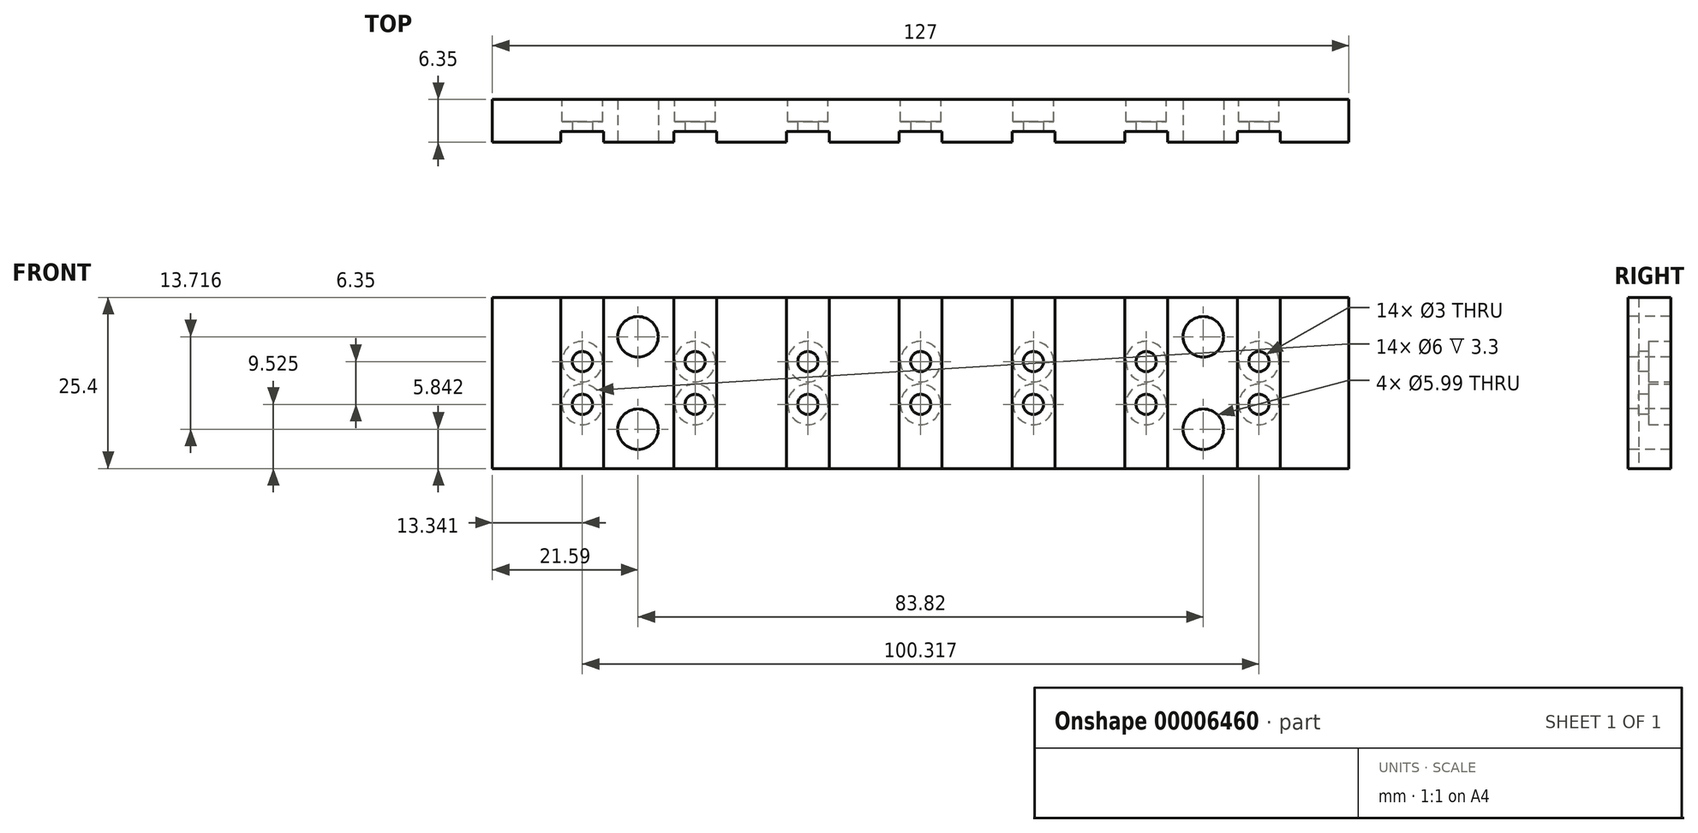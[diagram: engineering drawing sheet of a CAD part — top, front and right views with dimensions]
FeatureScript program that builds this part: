
annotation { "Feature Type Name" : "Feature", "Feature Type Description" : "" }
export const myFeature = defineFeature(function(context is Context, id is Id, definition is map)
    precondition{}
    {
        {
            var Q0;
            Q0=qCreatedBy(makeId("Front.planeOp"),FACE);
            var sketch = newSketch(context, id + "F0", { "sketchPlane" : qUnion([Q0])});
            skLineSegment(sketch, "E0.bottom", {"start": v(0, 0) * mm, "end": v(127, 0) * mm});
            skLineSegment(sketch, "E0.top", {"start": v(0, 25.4) * mm, "end": v(127, 25.4) * mm});
            skLineSegment(sketch, "E0.left", {"start": v(0, 0) * mm, "end": v(0, 25.4) * mm});
            skLineSegment(sketch, "E0.right", {"start": v(127, 0) * mm, "end": v(127, 25.4) * mm});
            skSolve(sketch);
        }
        {
            var Q0;
            Q0 = qSketchRegion(id + "F0", true);
            extrude(context, id + "F1", {"entities" : qUnion([Q0]), "depth" : 6.35 * mm});
        }
        {
            var Q0;
            Q0=makeQuery(id+"F1.opExtrude","CAP_FACE",FACE,{"disambiguationData":[OSD([sQuery(id+"F0.wireOp",EDGE,"E0.bottom"),sQuery(id+"F0.wireOp",EDGE,"E0.top"),sQuery(id+"F0.wireOp",EDGE,"E0.left"),sQuery(id+"F0.wireOp",EDGE,"E0.right")])],"isStart":false});
            var sketch = newSketch(context, id + "F2", { "sketchPlane" : qUnion([Q0])});
            skLineSegment(sketch, "E1.bottom", {"start": v(10.17, 25.4) * mm, "end": v(16.52, 25.4) * mm});
            skLineSegment(sketch, "E1.top", {"start": v(10.17, 0) * mm, "end": v(16.52, 0) * mm});
            skLineSegment(sketch, "E1.left", {"start": v(10.17, 25.4) * mm, "end": v(10.17, 0) * mm});
            skLineSegment(sketch, "E1.right", {"start": v(16.52, 25.4) * mm, "end": v(16.52, 0) * mm});
            skLineSegment(sketch, "E2.bottom", {"start": v(26.89, 25.4) * mm, "end": v(33.24, 25.4) * mm});
            skLineSegment(sketch, "E2.top", {"start": v(26.89, 0) * mm, "end": v(33.24, 0) * mm});
            skLineSegment(sketch, "E2.left", {"start": v(26.89, 25.4) * mm, "end": v(26.89, 0) * mm});
            skLineSegment(sketch, "E2.right", {"start": v(33.24, 25.4) * mm, "end": v(33.24, 0) * mm});
            skLineSegment(sketch, "E3.bottom", {"start": v(43.6, 25.4) * mm, "end": v(49.96, 25.4) * mm});
            skLineSegment(sketch, "E3.top", {"start": v(43.6, 0) * mm, "end": v(49.96, 0) * mm});
            skLineSegment(sketch, "E3.left", {"start": v(43.6, 25.4) * mm, "end": v(43.6, 0) * mm});
            skLineSegment(sketch, "E3.right", {"start": v(49.96, 25.4) * mm, "end": v(49.96, 0) * mm});
            skLineSegment(sketch, "E4.bottom", {"start": v(60.33, 25.4) * mm, "end": v(66.67, 25.4) * mm});
            skLineSegment(sketch, "E4.top", {"start": v(60.33, 0) * mm, "end": v(66.67, 0) * mm});
            skLineSegment(sketch, "E4.left", {"start": v(60.33, 25.4) * mm, "end": v(60.33, 0) * mm});
            skLineSegment(sketch, "E4.right", {"start": v(66.67, 25.4) * mm, "end": v(66.67, 0) * mm});
            skLineSegment(sketch, "E5.bottom", {"start": v(77.04, 25.4) * mm, "end": v(83.4, 25.4) * mm});
            skLineSegment(sketch, "E5.top", {"start": v(77.04, 0) * mm, "end": v(83.4, 0) * mm});
            skLineSegment(sketch, "E5.left", {"start": v(77.04, 25.4) * mm, "end": v(77.04, 0) * mm});
            skLineSegment(sketch, "E5.right", {"start": v(83.4, 25.4) * mm, "end": v(83.4, 0) * mm});
            skLineSegment(sketch, "E6.bottom", {"start": v(93.76, 25.4) * mm, "end": v(100.11, 25.4) * mm});
            skLineSegment(sketch, "E6.top", {"start": v(93.76, 0) * mm, "end": v(100.11, 0) * mm});
            skLineSegment(sketch, "E6.left", {"start": v(93.76, 25.4) * mm, "end": v(93.76, 0) * mm});
            skLineSegment(sketch, "E6.right", {"start": v(100.11, 25.4) * mm, "end": v(100.11, 0) * mm});
            skLineSegment(sketch, "E7.bottom", {"start": v(110.48, 25.4) * mm, "end": v(116.83, 25.4) * mm});
            skLineSegment(sketch, "E7.top", {"start": v(110.48, 0) * mm, "end": v(116.83, 0) * mm});
            skLineSegment(sketch, "E7.left", {"start": v(110.48, 25.4) * mm, "end": v(110.48, 0) * mm});
            skLineSegment(sketch, "E7.right", {"start": v(116.83, 25.4) * mm, "end": v(116.83, 0) * mm});
            skLineSegment(sketch, "E8", {"start": v(16.52, 25.4) * mm, "end": v(26.89, 25.4) * mm, "construction": true});
            skLineSegment(sketch, "E9", {"start": v(33.24, 25.4) * mm, "end": v(43.6, 25.4) * mm, "construction": true});
            skLineSegment(sketch, "E10", {"start": v(49.96, 25.4) * mm, "end": v(60.33, 25.4) * mm, "construction": true});
            skLineSegment(sketch, "E11", {"start": v(66.67, 25.4) * mm, "end": v(77.04, 25.4) * mm, "construction": true});
            skLineSegment(sketch, "E12", {"start": v(83.4, 25.4) * mm, "end": v(93.76, 25.4) * mm, "construction": true});
            skLineSegment(sketch, "E13", {"start": v(100.11, 25.4) * mm, "end": v(110.48, 25.4) * mm, "construction": true});
            skLineSegment(sketch, "E14", {"start": v(10.17, 25.4) * mm, "end": v(0, 25.4) * mm, "construction": true});
            skLineSegment(sketch, "E15", {"start": v(0, 25.4) * mm, "end": v(10.17, 25.4) * mm, "construction": true});
            skLineSegment(sketch, "E16", {"start": v(116.83, 25.4) * mm, "end": v(127, 25.4) * mm, "construction": true});
            skLineSegment(sketch, "E17", {"start": v(127, 25.4) * mm, "end": v(116.83, 25.4) * mm, "construction": true});
            skSolve(sketch);
        }
        {
            var Q0;
            Q0 = qSketchRegion(id + "F2", true);
            extrude(context, id + "F3", {"entities" : qUnion([Q0]), "operationType" : NewBodyOperationType.REMOVE, "oppositeDirection" : true, "depth" : 1.59 * mm});
        }
        {
            var Q0;
            Q0=makeQuery(id+"F3.boolean.opBoolean","COPY",FACE,{"derivedFrom":makeQuery(id+"F3.opExtrude","CAP_FACE",FACE,{"disambiguationData":[OSD([sQuery(id+"F2.wireOp",EDGE,"E1.bottom"),sQuery(id+"F2.wireOp",EDGE,"E1.top"),sQuery(id+"F2.wireOp",EDGE,"E1.left"),sQuery(id+"F2.wireOp",EDGE,"E1.right")])],"isStart":false})});
            var sketch = newSketch(context, id + "F4", { "sketchPlane" : qUnion([Q0])});
            skLineSegment(sketch, "E18", {"start": v(10.17, 12.7) * mm, "end": v(138.56, 12.7) * mm, "construction": true});
            skLineSegment(sketch, "E19", {"start": v(13.34, 12.7) * mm, "end": v(13.34, 15.88) * mm, "construction": true});
            skLineSegment(sketch, "E20", {"start": v(13.34, 12.7) * mm, "end": v(13.34, 9.52) * mm, "construction": true});
            skCircle(sketch, "E21", {"center": v(13.34, 15.88) * mm, "radius": 1.5 * mm});
            skCircle(sketch, "E22", {"center": v(13.34, 9.52) * mm, "radius": 1.5 * mm});
            skCircle(sketch, "E23.1.0.0", {"center": v(30.06, 15.88) * mm, "radius": 1.5 * mm});
            skLineSegment(sketch, "E23.1.0.1", {"start": v(30.06, 12.7) * mm, "end": v(30.06, 15.88) * mm, "construction": true});
            skCircle(sketch, "E23.1.0.2", {"center": v(30.06, 9.52) * mm, "radius": 1.5 * mm});
            skLineSegment(sketch, "E23.1.0.3", {"start": v(30.06, 12.7) * mm, "end": v(30.06, 9.52) * mm, "construction": true});
            skCircle(sketch, "E23.2.0.0", {"center": v(46.78, 15.88) * mm, "radius": 1.5 * mm});
            skLineSegment(sketch, "E23.2.0.1", {"start": v(46.78, 12.7) * mm, "end": v(46.78, 15.88) * mm, "construction": true});
            skCircle(sketch, "E23.2.0.2", {"center": v(46.78, 9.52) * mm, "radius": 1.5 * mm});
            skLineSegment(sketch, "E23.2.0.3", {"start": v(46.78, 12.7) * mm, "end": v(46.78, 9.52) * mm, "construction": true});
            skCircle(sketch, "E23.3.0.0", {"center": v(63.5, 15.88) * mm, "radius": 1.5 * mm});
            skLineSegment(sketch, "E23.3.0.1", {"start": v(63.5, 12.7) * mm, "end": v(63.5, 15.88) * mm, "construction": true});
            skCircle(sketch, "E23.3.0.2", {"center": v(63.5, 9.52) * mm, "radius": 1.5 * mm});
            skLineSegment(sketch, "E23.3.0.3", {"start": v(63.5, 12.7) * mm, "end": v(63.5, 9.52) * mm, "construction": true});
            skCircle(sketch, "E23.4.0.0", {"center": v(80.22, 15.88) * mm, "radius": 1.5 * mm});
            skLineSegment(sketch, "E23.4.0.1", {"start": v(80.22, 12.7) * mm, "end": v(80.22, 15.88) * mm, "construction": true});
            skCircle(sketch, "E23.4.0.2", {"center": v(80.22, 9.52) * mm, "radius": 1.5 * mm});
            skLineSegment(sketch, "E23.4.0.3", {"start": v(80.22, 12.7) * mm, "end": v(80.22, 9.52) * mm, "construction": true});
            skCircle(sketch, "E23.5.0.0", {"center": v(96.94, 15.88) * mm, "radius": 1.5 * mm});
            skLineSegment(sketch, "E23.5.0.1", {"start": v(96.94, 12.7) * mm, "end": v(96.94, 15.88) * mm, "construction": true});
            skCircle(sketch, "E23.5.0.2", {"center": v(96.94, 9.52) * mm, "radius": 1.5 * mm});
            skLineSegment(sketch, "E23.5.0.3", {"start": v(96.94, 12.7) * mm, "end": v(96.94, 9.52) * mm, "construction": true});
            skCircle(sketch, "E23.6.0.0", {"center": v(113.66, 15.88) * mm, "radius": 1.5 * mm});
            skLineSegment(sketch, "E23.6.0.1", {"start": v(113.66, 12.7) * mm, "end": v(113.66, 15.88) * mm, "construction": true});
            skCircle(sketch, "E23.6.0.2", {"center": v(113.66, 9.52) * mm, "radius": 1.5 * mm});
            skLineSegment(sketch, "E23.6.0.3", {"start": v(113.66, 12.7) * mm, "end": v(113.66, 9.52) * mm, "construction": true});
            skLineSegment(sketch, "E23.direction1", {"start": v(13.34, 15.88) * mm, "end": v(30.06, 15.88) * mm, "construction": true});
            skSolve(sketch);
        }
        {
            var Q0;
            Q0 = qSketchRegion(id + "F4", true);
            extrude(context, id + "F5", {"entities" : qUnion([Q0]), "operationType" : NewBodyOperationType.REMOVE, "endBound" : BoundingType.THROUGH_ALL, "oppositeDirection" : true, "depth" : 25.4 * mm});
        }
        {
            var Q0;
            Q0=makeQuery(id+"F1.opExtrude","CAP_FACE",FACE,{"disambiguationData":[OSD([sQuery(id+"F0.wireOp",EDGE,"E0.bottom"),sQuery(id+"F0.wireOp",EDGE,"E0.top"),sQuery(id+"F0.wireOp",EDGE,"E0.left"),sQuery(id+"F0.wireOp",EDGE,"E0.right")])],"isStart":true});
            var sketch = newSketch(context, id + "F6", { "sketchPlane" : qUnion([Q0])});
            skCircle(sketch, "E24", {"center": v(-113.66, 15.88) * mm, "radius": 3 * mm});
            skCircle(sketch, "E25.0.1.0", {"center": v(-113.66, 9.52) * mm, "radius": 3 * mm});
            skCircle(sketch, "E25.1.0.0", {"center": v(-96.94, 15.88) * mm, "radius": 3 * mm});
            skCircle(sketch, "E25.1.1.0", {"center": v(-96.94, 9.52) * mm, "radius": 3 * mm});
            skCircle(sketch, "E25.2.0.0", {"center": v(-80.22, 15.88) * mm, "radius": 3 * mm});
            skCircle(sketch, "E25.2.1.0", {"center": v(-80.22, 9.52) * mm, "radius": 3 * mm});
            skCircle(sketch, "E25.3.0.0", {"center": v(-63.5, 15.88) * mm, "radius": 3 * mm});
            skCircle(sketch, "E25.3.1.0", {"center": v(-63.5, 9.52) * mm, "radius": 3 * mm});
            skCircle(sketch, "E25.4.0.0", {"center": v(-46.78, 15.88) * mm, "radius": 3 * mm});
            skCircle(sketch, "E25.4.1.0", {"center": v(-46.78, 9.52) * mm, "radius": 3 * mm});
            skCircle(sketch, "E25.5.0.0", {"center": v(-30.06, 15.88) * mm, "radius": 3 * mm});
            skCircle(sketch, "E25.5.1.0", {"center": v(-30.06, 9.52) * mm, "radius": 3 * mm});
            skCircle(sketch, "E25.6.0.0", {"center": v(-13.34, 15.88) * mm, "radius": 3 * mm});
            skCircle(sketch, "E25.6.1.0", {"center": v(-13.34, 9.52) * mm, "radius": 3 * mm});
            skLineSegment(sketch, "E25.direction1", {"start": v(-113.66, 15.88) * mm, "end": v(-96.94, 15.88) * mm, "construction": true});
            skLineSegment(sketch, "E25.direction2", {"start": v(-113.66, 15.88) * mm, "end": v(-113.66, 9.52) * mm, "construction": true});
            skSolve(sketch);
        }
        {
            var Q0;
            Q0 = qSketchRegion(id + "F6", true);
            extrude(context, id + "F7", {"entities" : qUnion([Q0]), "operationType" : NewBodyOperationType.REMOVE, "oppositeDirection" : true, "depth" : 3.3 * mm});
        }
        {
            var Q0;
            {var subQ0=sQuery(id+"F0.wireOp",EDGE,"E0.bottom");var subQ1=sQuery(id+"F0.wireOp",EDGE,"E0.top");Q0=makeQuery(id+"F3.boolean.opBoolean","SPLIT",FACE,{"disambiguationData":[TD([makeQuery(id+"F3.opExtrude","SWEPT_FACE",FACE,{"disambiguationData":[OSD([sQuery(id+"F2.wireOp",EDGE,"E3.right")])]})])],"derivedFrom":makeQuery(id+"F1.opExtrude","CAP_FACE",FACE,{"disambiguationData":[OSD([subQ0,subQ1,sQuery(id+"F0.wireOp",EDGE,"E0.left"),sQuery(id+"F0.wireOp",EDGE,"E0.right")])],"isStart":false})});}
            var sketch = newSketch(context, id + "F8", { "sketchPlane" : qUnion([Q0])});
            skLineSegment(sketch, "E26.bottom", {"start": v(21.59, 19.56) * mm, "end": v(105.4, 19.56) * mm, "construction": true});
            skLineSegment(sketch, "E26.top", {"start": v(21.59, 5.84) * mm, "end": v(105.4, 5.84) * mm, "construction": true});
            skLineSegment(sketch, "E26.left", {"start": v(21.59, 19.56) * mm, "end": v(21.59, 5.84) * mm, "construction": true});
            skLineSegment(sketch, "E26.right", {"start": v(105.4, 19.56) * mm, "end": v(105.4, 5.84) * mm, "construction": true});
            skCircle(sketch, "E27", {"center": v(21.59, 19.56) * mm, "radius": 3 * mm});
            skCircle(sketch, "E28", {"center": v(21.59, 5.84) * mm, "radius": 3 * mm});
            skCircle(sketch, "E29", {"center": v(105.4, 5.84) * mm, "radius": 3 * mm});
            skCircle(sketch, "E30", {"center": v(105.4, 19.56) * mm, "radius": 3 * mm});
            skLineSegment(sketch, "E31", {"start": v(21.59, 12.7) * mm, "end": v(0, 12.7) * mm, "construction": true});
            skLineSegment(sketch, "E32", {"start": v(0, 0) * mm, "end": v(127, 0) * mm, "construction": true});
            skLineSegment(sketch, "E33", {"start": v(127, 0) * mm, "end": v(127, 25.4) * mm, "construction": true});
            skLineSegment(sketch, "E34", {"start": v(105.4, 12.7) * mm, "end": v(127, 12.7) * mm, "construction": true});
            skSolve(sketch);
        }
        {
            var Q0;
            Q0 = qSketchRegion(id + "F8", true);
            extrude(context, id + "F9", {"entities" : qUnion([Q0]), "operationType" : NewBodyOperationType.REMOVE, "endBound" : BoundingType.THROUGH_ALL, "oppositeDirection" : true, "depth" : 25.4 * mm});
        }
    });
